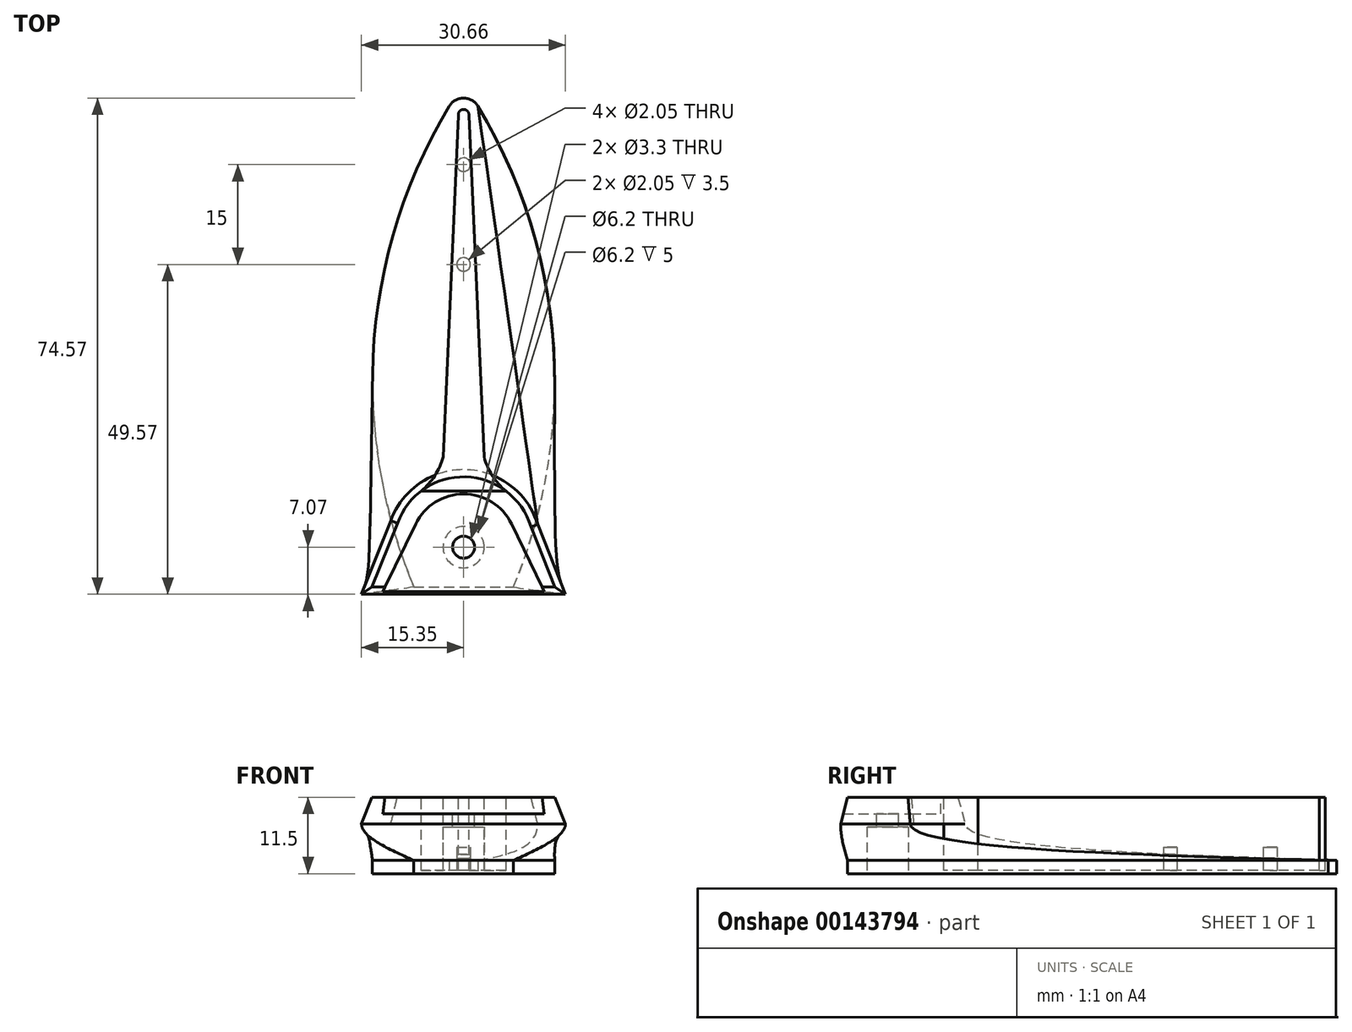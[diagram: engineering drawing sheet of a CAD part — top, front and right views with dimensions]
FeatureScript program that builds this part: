
annotation { "Feature Type Name" : "Feature", "Feature Type Description" : "" }
export const myFeature = defineFeature(function(context is Context, id is Id, definition is map)
    precondition{}
    {
        {
            var Q0;
            Q0=qCreatedBy(makeId("Top.planeOp"),FACE);
            var sketch = newSketch(context, id + "F0", { "sketchPlane" : qUnion([Q0])});
            skLineSegment(sketch, "E0", {"start": v(9.68, 4.17) * mm, "end": v(13.73, -6) * mm});
            skLineSegment(sketch, "E1", {"start": v(-9.84, 3.86) * mm, "end": v(-13.77, -6) * mm});
            skArc(sketch, "E2.trimOffspring", {"start": v(10.13, 3.06) * mm, "mid": v(0.29, 10.57) * mm, "end": v(-9.94, 3.6) * mm});
            skLineSegment(sketch, "E3", {"start": v(-13.77, -6) * mm, "end": v(13.73, -6) * mm});
            skCircle(sketch, "E4", {"center": v(0, 0) * mm, "radius": 1.65 * mm});
            skSolve(sketch);
        }
        {
            var Q0;
            {var subQ1=sQuery(id+"F0.wireOp",EDGE,"E2.trimOffspring");Q0=makeQuery(id+"F0.imprint","IMPRINT",FACE,{"disambiguationData":[TD([[makeQuery(id+"F0.imprint","IMPRINT",EDGE,{"derivedFrom":subQ1}),1.0]])]});}
            var Q1;
            Q1=makeQuery(id+"F0.imprint","IMPRINT",FACE,{"disambiguationData":[TD([[makeQuery(id+"F0.imprint","IMPRINT",EDGE,{"derivedFrom":sQuery(id+"F0.wireOp",EDGE,"E4")}),1.0]])]});
            extrude(context, id + "F1", {"entities" : qUnion([Q0, Q1]), "oppositeDirection" : true, "depth" : 4 * mm, "hasDraft" : true, "draftAngle" : 15 * degree});
        }
        {
            var Q0;
            Q0=qCreatedBy(makeId("Top.planeOp"),FACE);
            var sketch = newSketch(context, id + "F2", { "sketchPlane" : qUnion([Q0])});
            skPoint(sketch, "E5.middle", {"position": v(0, 0) * mm});
            skArc(sketch, "E6", {"start": v(7.2, 3.5) * mm, "mid": v(0, 8) * mm, "end": v(-7.2, 3.5) * mm});
            skLineSegment(sketch, "E7", {"start": v(-11.8, -6) * mm, "end": v(-7.2, 3.5) * mm});
            skLineSegment(sketch, "E8", {"start": v(11.8, -6) * mm, "end": v(7.2, 3.5) * mm});
            skLineSegment(sketch, "E9", {"start": v(11.8, -6) * mm, "end": v(12.73, -7.93) * mm});
            skLineSegment(sketch, "E10", {"start": v(-11.8, -6) * mm, "end": v(-12.73, -7.93) * mm});
            skLineSegment(sketch, "E11", {"start": v(12.73, -7.93) * mm, "end": v(-12.73, -7.93) * mm});
            skSolve(sketch);
        }
        {
            var Q0;
            Q0=makeQuery(id+"F2.imprint","IMPRINT",FACE,{"disambiguationData":[TD([[makeQuery(id+"F2.imprint","IMPRINT",EDGE,{"derivedFrom":sQuery(id+"F2.wireOp",EDGE,"E6")}),1.0]])]});
            extrude(context, id + "F3", {"entities" : qUnion([Q0]), "operationType" : NewBodyOperationType.REMOVE, "oppositeDirection" : true, "offsetDistance" : 25 * mm, "depth" : 2.5 * mm});
        }
        {
            var Q0;
            Q0=makeQuery(id+"F1.opExtrude","CAP_FACE",FACE,{"disambiguationData":[OSD([sQuery(id+"F0.wireOp",EDGE,"E0"),sQuery(id+"F0.wireOp",EDGE,"E1"),sQuery(id+"F0.wireOp",EDGE,"E2.trimOffspring"),sQuery(id+"F0.wireOp",EDGE,"E3"),sQuery(id+"F0.wireOp",EDGE,"E4")])],"isStart":false});
            cPlane(context, id + "F4", {"entities" : qUnion([Q0]), "cplaneType" : CPlaneType.OFFSET, "offset" : 7.5 * mm, "width" : 150 * mm, "height" : 150 * mm});
        }
        {
            var Q0;
            Q0=qCreatedBy(id+"F4.planeOp",FACE);
            var sketch = newSketch(context, id + "F5", { "sketchPlane" : qUnion([Q0])});
            skArc(sketch, "E12", {"start": v(-2.16, -66.26) * mm, "mid": v(0, -67.5) * mm, "end": v(2.16, -66.26) * mm});
            skArc(sketch, "E13", {"start": v(-7.5, 6) * mm, "mid": v(-13.48, -30.77) * mm, "end": v(-2.16, -66.26) * mm});
            skArc(sketch, "E14.MirrorCS", {"start": v(7.5, 6) * mm, "mid": v(13.48, -30.77) * mm, "end": v(2.16, -66.26) * mm});
            skLineSegment(sketch, "E15", {"start": v(-7.5, 6) * mm, "end": v(7.5, 6) * mm});
            skSolve(sketch);
        }
        {
            var Q0;
            Q0=makeQuery(id+"F5.imprint","IMPRINT",FACE,{"disambiguationData":[TD([[makeQuery(id+"F5.imprint","IMPRINT",EDGE,{"derivedFrom":sQuery(id+"F5.wireOp",EDGE,"E12")}),1.0]])]});
            extrude(context, id + "F6", {"entities" : qUnion([Q0]), "oppositeDirection" : true, "offsetDistance" : 25 * mm, "depth" : 2 * mm});
        }
        {
            var Q0;
            Q0=makeQuery(id+"F6.opExtrude","CAP_FACE",FACE,{"disambiguationData":[OSD([sQuery(id+"F5.wireOp",EDGE,"E12"),sQuery(id+"F5.wireOp",EDGE,"E13"),sQuery(id+"F5.wireOp",EDGE,"E14.MirrorCS"),sQuery(id+"F5.wireOp",EDGE,"E15")])],"isStart":false});
            var Q1;
            Q1=makeQuery(id+"F1.opExtrude","CAP_FACE",FACE,{"disambiguationData":[OSD([sQuery(id+"F0.wireOp",EDGE,"E0"),sQuery(id+"F0.wireOp",EDGE,"E1"),sQuery(id+"F0.wireOp",EDGE,"E2.trimOffspring"),sQuery(id+"F0.wireOp",EDGE,"E3"),sQuery(id+"F0.wireOp",EDGE,"E4")])],"isStart":false});
            var Q2;
            Q2=makeQuery(id+"F1.opExtrude","CAP_FACE",FACE,{"disambiguationData":[OSD([sQuery(id+"F0.wireOp",EDGE,"E0"),sQuery(id+"F0.wireOp",EDGE,"E1"),sQuery(id+"F0.wireOp",EDGE,"E2.trimOffspring"),sQuery(id+"F0.wireOp",EDGE,"E3"),sQuery(id+"F0.wireOp",EDGE,"E4")])],"isStart":false});
            var Q3;
            Q3=makeQuery(id+"F6.opExtrude","CAP_FACE",FACE,{"disambiguationData":[OSD([sQuery(id+"F5.wireOp",EDGE,"E12"),sQuery(id+"F5.wireOp",EDGE,"E13"),sQuery(id+"F5.wireOp",EDGE,"E14.MirrorCS"),sQuery(id+"F5.wireOp",EDGE,"E15")])],"isStart":false});
            var Q4;
            Q4=makeQuery(id+"F1.opExtrude","CAP_VERTEX",VERTEX,{"disambiguationData":[OSD([sQuery(id+"F0.wireOp",EDGE,"E0"),sQuery(id+"F0.wireOp",EDGE,"E3")])],"isStart":false});
            var Q5;
            Q5=makeQuery(id+"F6.opExtrude","CAP_VERTEX",VERTEX,{"disambiguationData":[OSD([sQuery(id+"F5.wireOp",EDGE,"E14.MirrorCS"),sQuery(id+"F5.wireOp",EDGE,"E15")])],"isStart":false});
            loft(context, id + "F7", {"endCondition" : LoftEndDerivativeType.NORMAL_TO_PROFILE, "endMagnitude" : 1, "sheetProfilesArray" : [{ "sheetProfileEntities" : qUnion([Q0]) }, { "sheetProfileEntities" : qUnion([Q1]) }], "wireProfilesArray" : [{ "wireProfileEntities" : qUnion([Q2]) }, { "wireProfileEntities" : qUnion([Q3]) }], "connections" : [{ "connectionEntities" : qUnion([Q4, Q5]), "connectionEdgeQueries" : qUnion([]), "connectionEdgeParameters" : [] }]});
        }
        {
            var Q0;
            Q0=makeQuery(id+"F3.boolean.opBoolean","COPY",FACE,{"derivedFrom":makeQuery(id+"F3.opExtrude","CAP_FACE",FACE,{"disambiguationData":[OSD([sQuery(id+"F2.wireOp",EDGE,"E6"),sQuery(id+"F2.wireOp",EDGE,"E7"),sQuery(id+"F2.wireOp",EDGE,"E8"),sQuery(id+"F2.wireOp",EDGE,"E9"),sQuery(id+"F2.wireOp",EDGE,"E10"),sQuery(id+"F2.wireOp",EDGE,"E11")])],"isStart":false})});
            var sketch = newSketch(context, id + "F8", { "sketchPlane" : qUnion([Q0])});
            skCircle(sketch, "E16", {"center": v(0, 0) * mm, "radius": 1.65 * mm});
            skSolve(sketch);
        }
        {
            var Q0;
            Q0=qSketchRegion(id+"F8",true);
            extrude(context, id + "F9", {"entities" : qUnion([Q0]), "operationType" : NewBodyOperationType.REMOVE, "oppositeDirection" : true, "offsetDistance" : 25 * mm, "depth" : 25 * mm});
        }
        {
            var Q0;
            Q0=makeQuery(id+"F1.opExtrude","CAP_FACE",FACE,{"disambiguationData":[OSD([sQuery(id+"F0.wireOp",EDGE,"E0"),sQuery(id+"F0.wireOp",EDGE,"E1"),sQuery(id+"F0.wireOp",EDGE,"E2.trimOffspring"),sQuery(id+"F0.wireOp",EDGE,"E3")])],"isStart":true});
            var sketch = newSketch(context, id + "F10", { "sketchPlane" : qUnion([Q0])});
            skArc(sketch, "E17", {"start": v(0.8, 64.89) * mm, "mid": v(0, 65.8) * mm, "end": v(-0.8, 64.89) * mm});
            skLineSegment(sketch, "E18", {"start": v(0.8, 64.89) * mm, "end": v(3.09, 13.6) * mm});
            skLineSegment(sketch, "E19.MirrorCS", {"start": v(-0.8, 64.89) * mm, "end": v(-3.09, 13.6) * mm});
            skArc(sketch, "E20", {"start": v(3.09, 13.6) * mm, "mid": v(4.32, 10.75) * mm, "end": v(6.38, 8.43) * mm});
            skLineSegment(sketch, "E21", {"start": v(0, 15.87) * mm, "end": v(0, 13.14) * mm, "construction": true});
            skArc(sketch, "E22.MirrorCS", {"start": v(-3.09, 13.6) * mm, "mid": v(-4.32, 10.75) * mm, "end": v(-6.38, 8.43) * mm});
            skLineSegment(sketch, "E23", {"start": v(6.38, 8.43) * mm, "end": v(-6.38, 8.43) * mm});
            skPoint(sketch, "E24.start.orphan", {"position": v(3.25, 10.07) * mm});
            skPoint(sketch, "E25.orphan", {"position": v(-3.25, 10.07) * mm});
            skSolve(sketch);
        }
        {
            var Q0;
            Q0 = qSketchRegion(id + "F10", true);
            extrude(context, id + "F11", {"entities" : qUnion([Q0]), "oppositeDirection" : true, "depth" : 11 * mm, "offsetDistance" : 25 * mm});
        }
        {
            var Q0;
            Q0=makeQuery(id+"F6.opExtrude","CAP_FACE",FACE,{"disambiguationData":[OSD([sQuery(id+"F5.wireOp",EDGE,"E12"),sQuery(id+"F5.wireOp",EDGE,"E13"),sQuery(id+"F5.wireOp",EDGE,"E14.MirrorCS"),sQuery(id+"F5.wireOp",EDGE,"E15")])],"isStart":true});
            var sketch = newSketch(context, id + "F12", { "sketchPlane" : qUnion([Q0])});
            skCircle(sketch, "E26", {"center": v(0, 0) * mm, "radius": 3.1 * mm});
            skSolve(sketch);
        }
        {
            var Q0;
            Q0=qSketchRegion(id+"F12",true);
            extrude(context, id + "F13", {"entities" : qUnion([Q0]), "operationType" : NewBodyOperationType.REMOVE, "oppositeDirection" : true, "offsetDistance" : 25 * mm, "depth" : 7 * mm});
        }
        {
            var Q0;
            Q0=makeQuery(id+"F5.imprint","IMPRINT",FACE,{"disambiguationData":[TD([[makeQuery(id+"F5.imprint","IMPRINT",EDGE,{"derivedFrom":sQuery(id+"F5.wireOp",EDGE,"E12")}),1.0]])]});
            var sketch = newSketch(context, id + "F14", { "sketchPlane" : qUnion([Q0])});
            skCircle(sketch, "E27", {"center": v(0, -57.5) * mm, "radius": 1.02 * mm});
            skCircle(sketch, "E28", {"center": v(0, -42.5) * mm, "radius": 1.02 * mm});
            skSolve(sketch);
        }
        {
            var Q0;
            Q0 = qSketchRegion(id + "F14", true);
            extrude(context, id + "F15", {"entities" : qUnion([Q0]), "operationType" : NewBodyOperationType.REMOVE, "oppositeDirection" : true, "depth" : 4 * mm, "offsetDistance" : 25 * mm});
        }
    });
